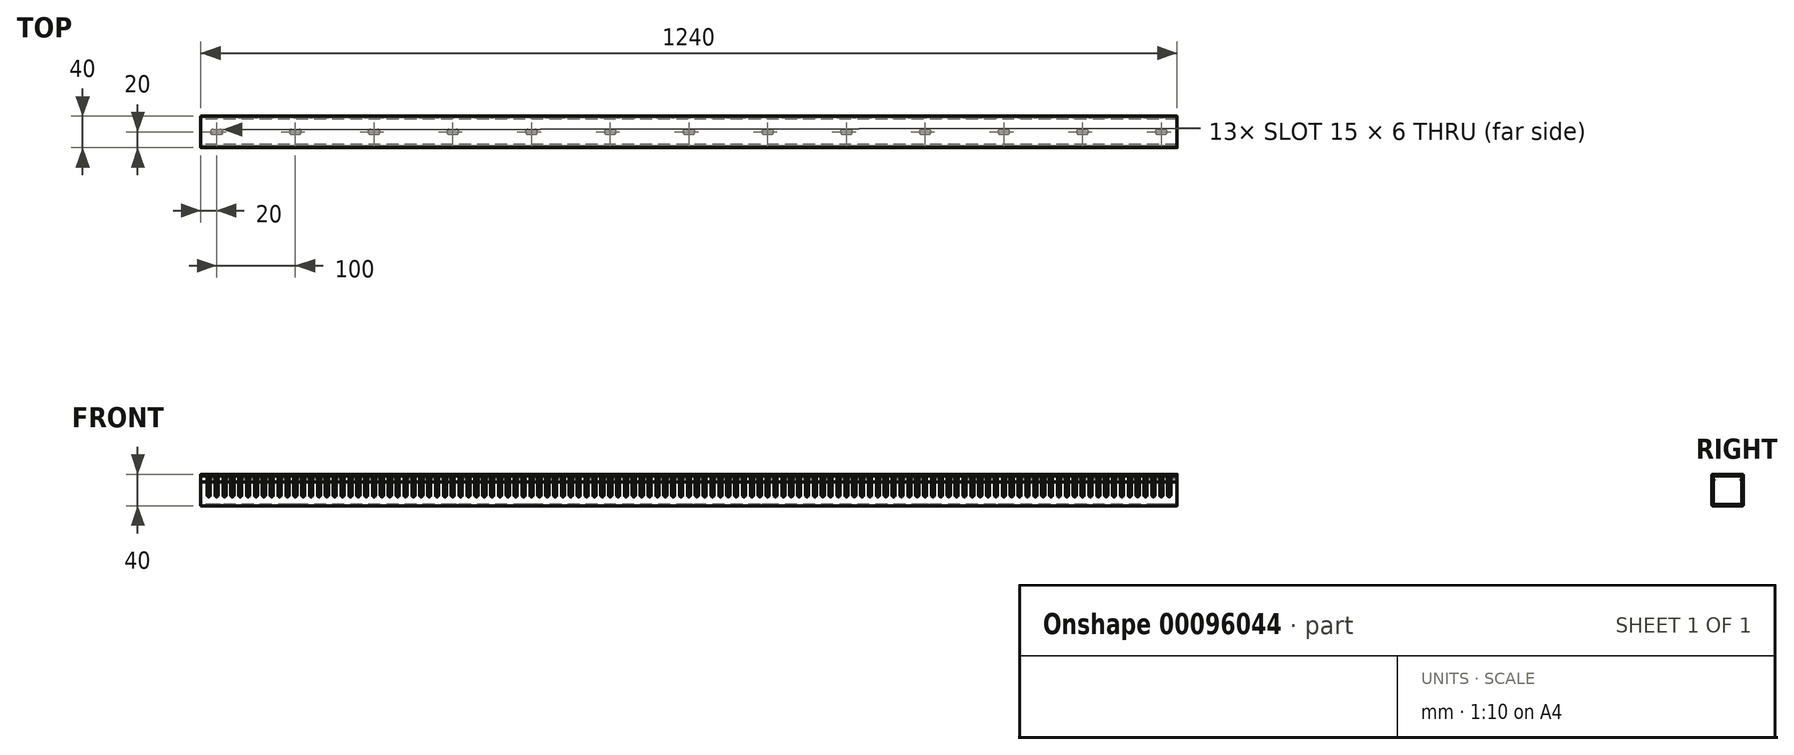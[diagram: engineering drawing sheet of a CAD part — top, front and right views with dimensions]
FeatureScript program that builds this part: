
annotation { "Feature Type Name" : "Feature", "Feature Type Description" : "" }
export const myFeature = defineFeature(function(context is Context, id is Id, definition is map)
    precondition{}
    {
        {
            var Q0;
            Q0=qCreatedBy(makeId("Right.planeOp"),FACE);
            var sketch = newSketch(context, id + "F0", { "sketchPlane" : qUnion([Q0])});
            skLineSegment(sketch, "E0", {"start": v(-20, 0) * mm, "end": v(-20, 38) * mm});
            skLineSegment(sketch, "E1", {"start": v(-20, 38) * mm, "end": v(-18, 38) * mm});
            skLineSegment(sketch, "E2", {"start": v(-18, 38) * mm, "end": v(-18, 2) * mm});
            skLineSegment(sketch, "E3", {"start": v(-18, 2) * mm, "end": v(18, 2) * mm});
            skLineSegment(sketch, "E4", {"start": v(18, 2) * mm, "end": v(18, 38) * mm});
            skLineSegment(sketch, "E5", {"start": v(18, 38) * mm, "end": v(20, 38) * mm});
            skLineSegment(sketch, "E6", {"start": v(20, 38) * mm, "end": v(20, 0) * mm});
            skLineSegment(sketch, "E7", {"start": v(20, 0) * mm, "end": v(-20, 0) * mm});
            skSolve(sketch);
        }
        {
            var Q0;
            Q0 = qSketchRegion(id + "F0", true);
            extrude(context, id + "F1", {"entities" : qUnion([Q0]), "endBound" : BoundingType.SYMMETRIC, "depth" : 1240 * mm});
        }
        {
            var Q0;
            Q0=makeQuery(id+"F1.opExtrude","SWEPT_FACE",FACE,{"disambiguationData":[OSD([sQuery(id+"F0.wireOp",EDGE,"E0")])]});
            var sketch = newSketch(context, id + "F2", { "sketchPlane" : qUnion([Q0])});
            skLineSegment(sketch, "E8.bottom", {"start": v(-2, 38) * mm, "end": v(2, 38) * mm});
            skLineSegment(sketch, "E8.left", {"start": v(-2, 38) * mm, "end": v(-2, 13.4) * mm});
            skLineSegment(sketch, "E8.right", {"start": v(2, 38) * mm, "end": v(2, 13.4) * mm});
            skArc(sketch, "E9", {"start": v(-2, 13.4) * mm, "mid": v(0, 11.4) * mm, "end": v(2, 13.4) * mm});
            skLineSegment(sketch, "E10.1.0.0", {"start": v(8, 38) * mm, "end": v(12, 38) * mm});
            skLineSegment(sketch, "E10.1.0.1", {"start": v(8, 38) * mm, "end": v(8, 13.4) * mm});
            skLineSegment(sketch, "E10.1.0.2", {"start": v(12, 38) * mm, "end": v(12, 13.4) * mm});
            skArc(sketch, "E10.1.0.3", {"start": v(8, 13.4) * mm, "mid": v(10, 11.4) * mm, "end": v(12, 13.4) * mm});
            skLineSegment(sketch, "E10.2.0.0", {"start": v(18, 38) * mm, "end": v(22, 38) * mm});
            skLineSegment(sketch, "E10.2.0.1", {"start": v(18, 38) * mm, "end": v(18, 13.4) * mm});
            skLineSegment(sketch, "E10.2.0.2", {"start": v(22, 38) * mm, "end": v(22, 13.4) * mm});
            skArc(sketch, "E10.2.0.3", {"start": v(18, 13.4) * mm, "mid": v(20, 11.4) * mm, "end": v(22, 13.4) * mm});
            skLineSegment(sketch, "E10.3.0.0", {"start": v(28, 38) * mm, "end": v(32, 38) * mm});
            skLineSegment(sketch, "E10.3.0.1", {"start": v(28, 38) * mm, "end": v(28, 13.4) * mm});
            skLineSegment(sketch, "E10.3.0.2", {"start": v(32, 38) * mm, "end": v(32, 13.4) * mm});
            skArc(sketch, "E10.3.0.3", {"start": v(28, 13.4) * mm, "mid": v(30, 11.4) * mm, "end": v(32, 13.4) * mm});
            skLineSegment(sketch, "E10.4.0.0", {"start": v(38, 38) * mm, "end": v(42, 38) * mm});
            skLineSegment(sketch, "E10.4.0.1", {"start": v(38, 38) * mm, "end": v(38, 13.4) * mm});
            skLineSegment(sketch, "E10.4.0.2", {"start": v(42, 38) * mm, "end": v(42, 13.4) * mm});
            skArc(sketch, "E10.4.0.3", {"start": v(38, 13.4) * mm, "mid": v(40, 11.4) * mm, "end": v(42, 13.4) * mm});
            skLineSegment(sketch, "E10.5.0.0", {"start": v(48, 38) * mm, "end": v(52, 38) * mm});
            skLineSegment(sketch, "E10.5.0.1", {"start": v(48, 38) * mm, "end": v(48, 13.4) * mm});
            skLineSegment(sketch, "E10.5.0.2", {"start": v(52, 38) * mm, "end": v(52, 13.4) * mm});
            skArc(sketch, "E10.5.0.3", {"start": v(48, 13.4) * mm, "mid": v(50, 11.4) * mm, "end": v(52, 13.4) * mm});
            skLineSegment(sketch, "E10.6.0.0", {"start": v(58, 38) * mm, "end": v(62, 38) * mm});
            skLineSegment(sketch, "E10.6.0.1", {"start": v(58, 38) * mm, "end": v(58, 13.4) * mm});
            skLineSegment(sketch, "E10.6.0.2", {"start": v(62, 38) * mm, "end": v(62, 13.4) * mm});
            skArc(sketch, "E10.6.0.3", {"start": v(58, 13.4) * mm, "mid": v(60, 11.4) * mm, "end": v(62, 13.4) * mm});
            skLineSegment(sketch, "E10.7.0.0", {"start": v(68, 38) * mm, "end": v(72, 38) * mm});
            skLineSegment(sketch, "E10.7.0.1", {"start": v(68, 38) * mm, "end": v(68, 13.4) * mm});
            skLineSegment(sketch, "E10.7.0.2", {"start": v(72, 38) * mm, "end": v(72, 13.4) * mm});
            skArc(sketch, "E10.7.0.3", {"start": v(68, 13.4) * mm, "mid": v(70, 11.4) * mm, "end": v(72, 13.4) * mm});
            skLineSegment(sketch, "E10.8.0.0", {"start": v(78, 38) * mm, "end": v(82, 38) * mm});
            skLineSegment(sketch, "E10.8.0.1", {"start": v(78, 38) * mm, "end": v(78, 13.4) * mm});
            skLineSegment(sketch, "E10.8.0.2", {"start": v(82, 38) * mm, "end": v(82, 13.4) * mm});
            skArc(sketch, "E10.8.0.3", {"start": v(78, 13.4) * mm, "mid": v(80, 11.4) * mm, "end": v(82, 13.4) * mm});
            skLineSegment(sketch, "E10.9.0.0", {"start": v(88, 38) * mm, "end": v(92, 38) * mm});
            skLineSegment(sketch, "E10.9.0.1", {"start": v(88, 38) * mm, "end": v(88, 13.4) * mm});
            skLineSegment(sketch, "E10.9.0.2", {"start": v(92, 38) * mm, "end": v(92, 13.4) * mm});
            skArc(sketch, "E10.9.0.3", {"start": v(88, 13.4) * mm, "mid": v(90, 11.4) * mm, "end": v(92, 13.4) * mm});
            skLineSegment(sketch, "E10.10.0.0", {"start": v(98, 38) * mm, "end": v(102, 38) * mm});
            skLineSegment(sketch, "E10.10.0.1", {"start": v(98, 38) * mm, "end": v(98, 13.4) * mm});
            skLineSegment(sketch, "E10.10.0.2", {"start": v(102, 38) * mm, "end": v(102, 13.4) * mm});
            skArc(sketch, "E10.10.0.3", {"start": v(98, 13.4) * mm, "mid": v(100, 11.4) * mm, "end": v(102, 13.4) * mm});
            skLineSegment(sketch, "E10.11.0.0", {"start": v(108, 38) * mm, "end": v(112, 38) * mm});
            skLineSegment(sketch, "E10.11.0.1", {"start": v(108, 38) * mm, "end": v(108, 13.4) * mm});
            skLineSegment(sketch, "E10.11.0.2", {"start": v(112, 38) * mm, "end": v(112, 13.4) * mm});
            skArc(sketch, "E10.11.0.3", {"start": v(108, 13.4) * mm, "mid": v(110, 11.4) * mm, "end": v(112, 13.4) * mm});
            skLineSegment(sketch, "E10.12.0.0", {"start": v(118, 38) * mm, "end": v(122, 38) * mm});
            skLineSegment(sketch, "E10.12.0.1", {"start": v(118, 38) * mm, "end": v(118, 13.4) * mm});
            skLineSegment(sketch, "E10.12.0.2", {"start": v(122, 38) * mm, "end": v(122, 13.4) * mm});
            skArc(sketch, "E10.12.0.3", {"start": v(118, 13.4) * mm, "mid": v(120, 11.4) * mm, "end": v(122, 13.4) * mm});
            skLineSegment(sketch, "E10.13.0.0", {"start": v(128, 38) * mm, "end": v(132, 38) * mm});
            skLineSegment(sketch, "E10.13.0.1", {"start": v(128, 38) * mm, "end": v(128, 13.4) * mm});
            skLineSegment(sketch, "E10.13.0.2", {"start": v(132, 38) * mm, "end": v(132, 13.4) * mm});
            skArc(sketch, "E10.13.0.3", {"start": v(128, 13.4) * mm, "mid": v(130, 11.4) * mm, "end": v(132, 13.4) * mm});
            skLineSegment(sketch, "E10.14.0.0", {"start": v(138, 38) * mm, "end": v(142, 38) * mm});
            skLineSegment(sketch, "E10.14.0.1", {"start": v(138, 38) * mm, "end": v(138, 13.4) * mm});
            skLineSegment(sketch, "E10.14.0.2", {"start": v(142, 38) * mm, "end": v(142, 13.4) * mm});
            skArc(sketch, "E10.14.0.3", {"start": v(138, 13.4) * mm, "mid": v(140, 11.4) * mm, "end": v(142, 13.4) * mm});
            skLineSegment(sketch, "E10.15.0.0", {"start": v(148, 38) * mm, "end": v(152, 38) * mm});
            skLineSegment(sketch, "E10.15.0.1", {"start": v(148, 38) * mm, "end": v(148, 13.4) * mm});
            skLineSegment(sketch, "E10.15.0.2", {"start": v(152, 38) * mm, "end": v(152, 13.4) * mm});
            skArc(sketch, "E10.15.0.3", {"start": v(148, 13.4) * mm, "mid": v(150, 11.4) * mm, "end": v(152, 13.4) * mm});
            skLineSegment(sketch, "E10.16.0.0", {"start": v(158, 38) * mm, "end": v(162, 38) * mm});
            skLineSegment(sketch, "E10.16.0.1", {"start": v(158, 38) * mm, "end": v(158, 13.4) * mm});
            skLineSegment(sketch, "E10.16.0.2", {"start": v(162, 38) * mm, "end": v(162, 13.4) * mm});
            skArc(sketch, "E10.16.0.3", {"start": v(158, 13.4) * mm, "mid": v(160, 11.4) * mm, "end": v(162, 13.4) * mm});
            skLineSegment(sketch, "E10.17.0.0", {"start": v(168, 38) * mm, "end": v(172, 38) * mm});
            skLineSegment(sketch, "E10.17.0.1", {"start": v(168, 38) * mm, "end": v(168, 13.4) * mm});
            skLineSegment(sketch, "E10.17.0.2", {"start": v(172, 38) * mm, "end": v(172, 13.4) * mm});
            skArc(sketch, "E10.17.0.3", {"start": v(168, 13.4) * mm, "mid": v(170, 11.4) * mm, "end": v(172, 13.4) * mm});
            skLineSegment(sketch, "E10.18.0.0", {"start": v(178, 38) * mm, "end": v(182, 38) * mm});
            skLineSegment(sketch, "E10.18.0.1", {"start": v(178, 38) * mm, "end": v(178, 13.4) * mm});
            skLineSegment(sketch, "E10.18.0.2", {"start": v(182, 38) * mm, "end": v(182, 13.4) * mm});
            skArc(sketch, "E10.18.0.3", {"start": v(178, 13.4) * mm, "mid": v(180, 11.4) * mm, "end": v(182, 13.4) * mm});
            skLineSegment(sketch, "E10.19.0.0", {"start": v(188, 38) * mm, "end": v(192, 38) * mm});
            skLineSegment(sketch, "E10.19.0.1", {"start": v(188, 38) * mm, "end": v(188, 13.4) * mm});
            skLineSegment(sketch, "E10.19.0.2", {"start": v(192, 38) * mm, "end": v(192, 13.4) * mm});
            skArc(sketch, "E10.19.0.3", {"start": v(188, 13.4) * mm, "mid": v(190, 11.4) * mm, "end": v(192, 13.4) * mm});
            skLineSegment(sketch, "E10.20.0.0", {"start": v(198, 38) * mm, "end": v(202, 38) * mm});
            skLineSegment(sketch, "E10.20.0.1", {"start": v(198, 38) * mm, "end": v(198, 13.4) * mm});
            skLineSegment(sketch, "E10.20.0.2", {"start": v(202, 38) * mm, "end": v(202, 13.4) * mm});
            skArc(sketch, "E10.20.0.3", {"start": v(198, 13.4) * mm, "mid": v(200, 11.4) * mm, "end": v(202, 13.4) * mm});
            skLineSegment(sketch, "E10.21.0.0", {"start": v(208, 38) * mm, "end": v(212, 38) * mm});
            skLineSegment(sketch, "E10.21.0.1", {"start": v(208, 38) * mm, "end": v(208, 13.4) * mm});
            skLineSegment(sketch, "E10.21.0.2", {"start": v(212, 38) * mm, "end": v(212, 13.4) * mm});
            skArc(sketch, "E10.21.0.3", {"start": v(208, 13.4) * mm, "mid": v(210, 11.4) * mm, "end": v(212, 13.4) * mm});
            skLineSegment(sketch, "E10.22.0.0", {"start": v(218, 38) * mm, "end": v(222, 38) * mm});
            skLineSegment(sketch, "E10.22.0.1", {"start": v(218, 38) * mm, "end": v(218, 13.4) * mm});
            skLineSegment(sketch, "E10.22.0.2", {"start": v(222, 38) * mm, "end": v(222, 13.4) * mm});
            skArc(sketch, "E10.22.0.3", {"start": v(218, 13.4) * mm, "mid": v(220, 11.4) * mm, "end": v(222, 13.4) * mm});
            skLineSegment(sketch, "E10.23.0.0", {"start": v(228, 38) * mm, "end": v(232, 38) * mm});
            skLineSegment(sketch, "E10.23.0.1", {"start": v(228, 38) * mm, "end": v(228, 13.4) * mm});
            skLineSegment(sketch, "E10.23.0.2", {"start": v(232, 38) * mm, "end": v(232, 13.4) * mm});
            skArc(sketch, "E10.23.0.3", {"start": v(228, 13.4) * mm, "mid": v(230, 11.4) * mm, "end": v(232, 13.4) * mm});
            skLineSegment(sketch, "E10.24.0.0", {"start": v(238, 38) * mm, "end": v(242, 38) * mm});
            skLineSegment(sketch, "E10.24.0.1", {"start": v(238, 38) * mm, "end": v(238, 13.4) * mm});
            skLineSegment(sketch, "E10.24.0.2", {"start": v(242, 38) * mm, "end": v(242, 13.4) * mm});
            skArc(sketch, "E10.24.0.3", {"start": v(238, 13.4) * mm, "mid": v(240, 11.4) * mm, "end": v(242, 13.4) * mm});
            skLineSegment(sketch, "E10.25.0.0", {"start": v(248, 38) * mm, "end": v(252, 38) * mm});
            skLineSegment(sketch, "E10.25.0.1", {"start": v(248, 38) * mm, "end": v(248, 13.4) * mm});
            skLineSegment(sketch, "E10.25.0.2", {"start": v(252, 38) * mm, "end": v(252, 13.4) * mm});
            skArc(sketch, "E10.25.0.3", {"start": v(248, 13.4) * mm, "mid": v(250, 11.4) * mm, "end": v(252, 13.4) * mm});
            skLineSegment(sketch, "E10.26.0.0", {"start": v(258, 38) * mm, "end": v(262, 38) * mm});
            skLineSegment(sketch, "E10.26.0.1", {"start": v(258, 38) * mm, "end": v(258, 13.4) * mm});
            skLineSegment(sketch, "E10.26.0.2", {"start": v(262, 38) * mm, "end": v(262, 13.4) * mm});
            skArc(sketch, "E10.26.0.3", {"start": v(258, 13.4) * mm, "mid": v(260, 11.4) * mm, "end": v(262, 13.4) * mm});
            skLineSegment(sketch, "E10.27.0.0", {"start": v(268, 38) * mm, "end": v(272, 38) * mm});
            skLineSegment(sketch, "E10.27.0.1", {"start": v(268, 38) * mm, "end": v(268, 13.4) * mm});
            skLineSegment(sketch, "E10.27.0.2", {"start": v(272, 38) * mm, "end": v(272, 13.4) * mm});
            skArc(sketch, "E10.27.0.3", {"start": v(268, 13.4) * mm, "mid": v(270, 11.4) * mm, "end": v(272, 13.4) * mm});
            skLineSegment(sketch, "E10.28.0.0", {"start": v(278, 38) * mm, "end": v(282, 38) * mm});
            skLineSegment(sketch, "E10.28.0.1", {"start": v(278, 38) * mm, "end": v(278, 13.4) * mm});
            skLineSegment(sketch, "E10.28.0.2", {"start": v(282, 38) * mm, "end": v(282, 13.4) * mm});
            skArc(sketch, "E10.28.0.3", {"start": v(278, 13.4) * mm, "mid": v(280, 11.4) * mm, "end": v(282, 13.4) * mm});
            skLineSegment(sketch, "E10.29.0.0", {"start": v(288, 38) * mm, "end": v(292, 38) * mm});
            skLineSegment(sketch, "E10.29.0.1", {"start": v(288, 38) * mm, "end": v(288, 13.4) * mm});
            skLineSegment(sketch, "E10.29.0.2", {"start": v(292, 38) * mm, "end": v(292, 13.4) * mm});
            skArc(sketch, "E10.29.0.3", {"start": v(288, 13.4) * mm, "mid": v(290, 11.4) * mm, "end": v(292, 13.4) * mm});
            skLineSegment(sketch, "E10.30.0.0", {"start": v(298, 38) * mm, "end": v(302, 38) * mm});
            skLineSegment(sketch, "E10.30.0.1", {"start": v(298, 38) * mm, "end": v(298, 13.4) * mm});
            skLineSegment(sketch, "E10.30.0.2", {"start": v(302, 38) * mm, "end": v(302, 13.4) * mm});
            skArc(sketch, "E10.30.0.3", {"start": v(298, 13.4) * mm, "mid": v(300, 11.4) * mm, "end": v(302, 13.4) * mm});
            skLineSegment(sketch, "E10.31.0.0", {"start": v(308, 38) * mm, "end": v(312, 38) * mm});
            skLineSegment(sketch, "E10.31.0.1", {"start": v(308, 38) * mm, "end": v(308, 13.4) * mm});
            skLineSegment(sketch, "E10.31.0.2", {"start": v(312, 38) * mm, "end": v(312, 13.4) * mm});
            skArc(sketch, "E10.31.0.3", {"start": v(308, 13.4) * mm, "mid": v(310, 11.4) * mm, "end": v(312, 13.4) * mm});
            skLineSegment(sketch, "E10.32.0.0", {"start": v(318, 38) * mm, "end": v(322, 38) * mm});
            skLineSegment(sketch, "E10.32.0.1", {"start": v(318, 38) * mm, "end": v(318, 13.4) * mm});
            skLineSegment(sketch, "E10.32.0.2", {"start": v(322, 38) * mm, "end": v(322, 13.4) * mm});
            skArc(sketch, "E10.32.0.3", {"start": v(318, 13.4) * mm, "mid": v(320, 11.4) * mm, "end": v(322, 13.4) * mm});
            skLineSegment(sketch, "E10.33.0.0", {"start": v(328, 38) * mm, "end": v(332, 38) * mm});
            skLineSegment(sketch, "E10.33.0.1", {"start": v(328, 38) * mm, "end": v(328, 13.4) * mm});
            skLineSegment(sketch, "E10.33.0.2", {"start": v(332, 38) * mm, "end": v(332, 13.4) * mm});
            skArc(sketch, "E10.33.0.3", {"start": v(328, 13.4) * mm, "mid": v(330, 11.4) * mm, "end": v(332, 13.4) * mm});
            skLineSegment(sketch, "E10.34.0.0", {"start": v(338, 38) * mm, "end": v(342, 38) * mm});
            skLineSegment(sketch, "E10.34.0.1", {"start": v(338, 38) * mm, "end": v(338, 13.4) * mm});
            skLineSegment(sketch, "E10.34.0.2", {"start": v(342, 38) * mm, "end": v(342, 13.4) * mm});
            skArc(sketch, "E10.34.0.3", {"start": v(338, 13.4) * mm, "mid": v(340, 11.4) * mm, "end": v(342, 13.4) * mm});
            skLineSegment(sketch, "E10.35.0.0", {"start": v(348, 38) * mm, "end": v(352, 38) * mm});
            skLineSegment(sketch, "E10.35.0.1", {"start": v(348, 38) * mm, "end": v(348, 13.4) * mm});
            skLineSegment(sketch, "E10.35.0.2", {"start": v(352, 38) * mm, "end": v(352, 13.4) * mm});
            skArc(sketch, "E10.35.0.3", {"start": v(348, 13.4) * mm, "mid": v(350, 11.4) * mm, "end": v(352, 13.4) * mm});
            skLineSegment(sketch, "E10.36.0.0", {"start": v(358, 38) * mm, "end": v(362, 38) * mm});
            skLineSegment(sketch, "E10.36.0.1", {"start": v(358, 38) * mm, "end": v(358, 13.4) * mm});
            skLineSegment(sketch, "E10.36.0.2", {"start": v(362, 38) * mm, "end": v(362, 13.4) * mm});
            skArc(sketch, "E10.36.0.3", {"start": v(358, 13.4) * mm, "mid": v(360, 11.4) * mm, "end": v(362, 13.4) * mm});
            skLineSegment(sketch, "E10.37.0.0", {"start": v(368, 38) * mm, "end": v(372, 38) * mm});
            skLineSegment(sketch, "E10.37.0.1", {"start": v(368, 38) * mm, "end": v(368, 13.4) * mm});
            skLineSegment(sketch, "E10.37.0.2", {"start": v(372, 38) * mm, "end": v(372, 13.4) * mm});
            skArc(sketch, "E10.37.0.3", {"start": v(368, 13.4) * mm, "mid": v(370, 11.4) * mm, "end": v(372, 13.4) * mm});
            skLineSegment(sketch, "E10.38.0.0", {"start": v(378, 38) * mm, "end": v(382, 38) * mm});
            skLineSegment(sketch, "E10.38.0.1", {"start": v(378, 38) * mm, "end": v(378, 13.4) * mm});
            skLineSegment(sketch, "E10.38.0.2", {"start": v(382, 38) * mm, "end": v(382, 13.4) * mm});
            skArc(sketch, "E10.38.0.3", {"start": v(378, 13.4) * mm, "mid": v(380, 11.4) * mm, "end": v(382, 13.4) * mm});
            skLineSegment(sketch, "E10.39.0.0", {"start": v(388, 38) * mm, "end": v(392, 38) * mm});
            skLineSegment(sketch, "E10.39.0.1", {"start": v(388, 38) * mm, "end": v(388, 13.4) * mm});
            skLineSegment(sketch, "E10.39.0.2", {"start": v(392, 38) * mm, "end": v(392, 13.4) * mm});
            skArc(sketch, "E10.39.0.3", {"start": v(388, 13.4) * mm, "mid": v(390, 11.4) * mm, "end": v(392, 13.4) * mm});
            skLineSegment(sketch, "E10.40.0.0", {"start": v(398, 38) * mm, "end": v(402, 38) * mm});
            skLineSegment(sketch, "E10.40.0.1", {"start": v(398, 38) * mm, "end": v(398, 13.4) * mm});
            skLineSegment(sketch, "E10.40.0.2", {"start": v(402, 38) * mm, "end": v(402, 13.4) * mm});
            skArc(sketch, "E10.40.0.3", {"start": v(398, 13.4) * mm, "mid": v(400, 11.4) * mm, "end": v(402, 13.4) * mm});
            skLineSegment(sketch, "E10.41.0.0", {"start": v(408, 38) * mm, "end": v(412, 38) * mm});
            skLineSegment(sketch, "E10.41.0.1", {"start": v(408, 38) * mm, "end": v(408, 13.4) * mm});
            skLineSegment(sketch, "E10.41.0.2", {"start": v(412, 38) * mm, "end": v(412, 13.4) * mm});
            skArc(sketch, "E10.41.0.3", {"start": v(408, 13.4) * mm, "mid": v(410, 11.4) * mm, "end": v(412, 13.4) * mm});
            skLineSegment(sketch, "E10.42.0.0", {"start": v(418, 38) * mm, "end": v(422, 38) * mm});
            skLineSegment(sketch, "E10.42.0.1", {"start": v(418, 38) * mm, "end": v(418, 13.4) * mm});
            skLineSegment(sketch, "E10.42.0.2", {"start": v(422, 38) * mm, "end": v(422, 13.4) * mm});
            skArc(sketch, "E10.42.0.3", {"start": v(418, 13.4) * mm, "mid": v(420, 11.4) * mm, "end": v(422, 13.4) * mm});
            skLineSegment(sketch, "E10.43.0.0", {"start": v(428, 38) * mm, "end": v(432, 38) * mm});
            skLineSegment(sketch, "E10.43.0.1", {"start": v(428, 38) * mm, "end": v(428, 13.4) * mm});
            skLineSegment(sketch, "E10.43.0.2", {"start": v(432, 38) * mm, "end": v(432, 13.4) * mm});
            skArc(sketch, "E10.43.0.3", {"start": v(428, 13.4) * mm, "mid": v(430, 11.4) * mm, "end": v(432, 13.4) * mm});
            skLineSegment(sketch, "E10.44.0.0", {"start": v(438, 38) * mm, "end": v(442, 38) * mm});
            skLineSegment(sketch, "E10.44.0.1", {"start": v(438, 38) * mm, "end": v(438, 13.4) * mm});
            skLineSegment(sketch, "E10.44.0.2", {"start": v(442, 38) * mm, "end": v(442, 13.4) * mm});
            skArc(sketch, "E10.44.0.3", {"start": v(438, 13.4) * mm, "mid": v(440, 11.4) * mm, "end": v(442, 13.4) * mm});
            skLineSegment(sketch, "E10.45.0.0", {"start": v(448, 38) * mm, "end": v(452, 38) * mm});
            skLineSegment(sketch, "E10.45.0.1", {"start": v(448, 38) * mm, "end": v(448, 13.4) * mm});
            skLineSegment(sketch, "E10.45.0.2", {"start": v(452, 38) * mm, "end": v(452, 13.4) * mm});
            skArc(sketch, "E10.45.0.3", {"start": v(448, 13.4) * mm, "mid": v(450, 11.4) * mm, "end": v(452, 13.4) * mm});
            skLineSegment(sketch, "E10.46.0.0", {"start": v(458, 38) * mm, "end": v(462, 38) * mm});
            skLineSegment(sketch, "E10.46.0.1", {"start": v(458, 38) * mm, "end": v(458, 13.4) * mm});
            skLineSegment(sketch, "E10.46.0.2", {"start": v(462, 38) * mm, "end": v(462, 13.4) * mm});
            skArc(sketch, "E10.46.0.3", {"start": v(458, 13.4) * mm, "mid": v(460, 11.4) * mm, "end": v(462, 13.4) * mm});
            skLineSegment(sketch, "E10.47.0.0", {"start": v(468, 38) * mm, "end": v(472, 38) * mm});
            skLineSegment(sketch, "E10.47.0.1", {"start": v(468, 38) * mm, "end": v(468, 13.4) * mm});
            skLineSegment(sketch, "E10.47.0.2", {"start": v(472, 38) * mm, "end": v(472, 13.4) * mm});
            skArc(sketch, "E10.47.0.3", {"start": v(468, 13.4) * mm, "mid": v(470, 11.4) * mm, "end": v(472, 13.4) * mm});
            skLineSegment(sketch, "E10.48.0.0", {"start": v(478, 38) * mm, "end": v(482, 38) * mm});
            skLineSegment(sketch, "E10.48.0.1", {"start": v(478, 38) * mm, "end": v(478, 13.4) * mm});
            skLineSegment(sketch, "E10.48.0.2", {"start": v(482, 38) * mm, "end": v(482, 13.4) * mm});
            skArc(sketch, "E10.48.0.3", {"start": v(478, 13.4) * mm, "mid": v(480, 11.4) * mm, "end": v(482, 13.4) * mm});
            skLineSegment(sketch, "E10.49.0.0", {"start": v(488, 38) * mm, "end": v(492, 38) * mm});
            skLineSegment(sketch, "E10.49.0.1", {"start": v(488, 38) * mm, "end": v(488, 13.4) * mm});
            skLineSegment(sketch, "E10.49.0.2", {"start": v(492, 38) * mm, "end": v(492, 13.4) * mm});
            skArc(sketch, "E10.49.0.3", {"start": v(488, 13.4) * mm, "mid": v(490, 11.4) * mm, "end": v(492, 13.4) * mm});
            skLineSegment(sketch, "E10.direction1", {"start": v(-2, 38) * mm, "end": v(8, 38) * mm, "construction": true});
            skLineSegment(sketch, "E11.1.0.0", {"start": v(-12, 38) * mm, "end": v(-8, 38) * mm});
            skLineSegment(sketch, "E11.1.0.1", {"start": v(-12, 38) * mm, "end": v(-12, 13.4) * mm});
            skLineSegment(sketch, "E11.1.0.2", {"start": v(-8, 38) * mm, "end": v(-8, 13.4) * mm});
            skArc(sketch, "E11.1.0.3", {"start": v(-12, 13.4) * mm, "mid": v(-10, 11.4) * mm, "end": v(-8, 13.4) * mm});
            skLineSegment(sketch, "E11.2.0.0", {"start": v(-22, 38) * mm, "end": v(-18, 38) * mm});
            skLineSegment(sketch, "E11.2.0.1", {"start": v(-22, 38) * mm, "end": v(-22, 13.4) * mm});
            skLineSegment(sketch, "E11.2.0.2", {"start": v(-18, 38) * mm, "end": v(-18, 13.4) * mm});
            skArc(sketch, "E11.2.0.3", {"start": v(-22, 13.4) * mm, "mid": v(-20, 11.4) * mm, "end": v(-18, 13.4) * mm});
            skLineSegment(sketch, "E11.3.0.0", {"start": v(-32, 38) * mm, "end": v(-28, 38) * mm});
            skLineSegment(sketch, "E11.3.0.1", {"start": v(-32, 38) * mm, "end": v(-32, 13.4) * mm});
            skLineSegment(sketch, "E11.3.0.2", {"start": v(-28, 38) * mm, "end": v(-28, 13.4) * mm});
            skArc(sketch, "E11.3.0.3", {"start": v(-32, 13.4) * mm, "mid": v(-30, 11.4) * mm, "end": v(-28, 13.4) * mm});
            skLineSegment(sketch, "E11.4.0.0", {"start": v(-42, 38) * mm, "end": v(-38, 38) * mm});
            skLineSegment(sketch, "E11.4.0.1", {"start": v(-42, 38) * mm, "end": v(-42, 13.4) * mm});
            skLineSegment(sketch, "E11.4.0.2", {"start": v(-38, 38) * mm, "end": v(-38, 13.4) * mm});
            skArc(sketch, "E11.4.0.3", {"start": v(-42, 13.4) * mm, "mid": v(-40, 11.4) * mm, "end": v(-38, 13.4) * mm});
            skLineSegment(sketch, "E11.5.0.0", {"start": v(-52, 38) * mm, "end": v(-48, 38) * mm});
            skLineSegment(sketch, "E11.5.0.1", {"start": v(-52, 38) * mm, "end": v(-52, 13.4) * mm});
            skLineSegment(sketch, "E11.5.0.2", {"start": v(-48, 38) * mm, "end": v(-48, 13.4) * mm});
            skArc(sketch, "E11.5.0.3", {"start": v(-52, 13.4) * mm, "mid": v(-50, 11.4) * mm, "end": v(-48, 13.4) * mm});
            skLineSegment(sketch, "E11.6.0.0", {"start": v(-62, 38) * mm, "end": v(-58, 38) * mm});
            skLineSegment(sketch, "E11.6.0.1", {"start": v(-62, 38) * mm, "end": v(-62, 13.4) * mm});
            skLineSegment(sketch, "E11.6.0.2", {"start": v(-58, 38) * mm, "end": v(-58, 13.4) * mm});
            skArc(sketch, "E11.6.0.3", {"start": v(-62, 13.4) * mm, "mid": v(-60, 11.4) * mm, "end": v(-58, 13.4) * mm});
            skLineSegment(sketch, "E11.7.0.0", {"start": v(-72, 38) * mm, "end": v(-68, 38) * mm});
            skLineSegment(sketch, "E11.7.0.1", {"start": v(-72, 38) * mm, "end": v(-72, 13.4) * mm});
            skLineSegment(sketch, "E11.7.0.2", {"start": v(-68, 38) * mm, "end": v(-68, 13.4) * mm});
            skArc(sketch, "E11.7.0.3", {"start": v(-72, 13.4) * mm, "mid": v(-70, 11.4) * mm, "end": v(-68, 13.4) * mm});
            skLineSegment(sketch, "E11.8.0.0", {"start": v(-82, 38) * mm, "end": v(-78, 38) * mm});
            skLineSegment(sketch, "E11.8.0.1", {"start": v(-82, 38) * mm, "end": v(-82, 13.4) * mm});
            skLineSegment(sketch, "E11.8.0.2", {"start": v(-78, 38) * mm, "end": v(-78, 13.4) * mm});
            skArc(sketch, "E11.8.0.3", {"start": v(-82, 13.4) * mm, "mid": v(-80, 11.4) * mm, "end": v(-78, 13.4) * mm});
            skLineSegment(sketch, "E11.9.0.0", {"start": v(-92, 38) * mm, "end": v(-88, 38) * mm});
            skLineSegment(sketch, "E11.9.0.1", {"start": v(-92, 38) * mm, "end": v(-92, 13.4) * mm});
            skLineSegment(sketch, "E11.9.0.2", {"start": v(-88, 38) * mm, "end": v(-88, 13.4) * mm});
            skArc(sketch, "E11.9.0.3", {"start": v(-92, 13.4) * mm, "mid": v(-90, 11.4) * mm, "end": v(-88, 13.4) * mm});
            skLineSegment(sketch, "E11.10.0.0", {"start": v(-102, 38) * mm, "end": v(-98, 38) * mm});
            skLineSegment(sketch, "E11.10.0.1", {"start": v(-102, 38) * mm, "end": v(-102, 13.4) * mm});
            skLineSegment(sketch, "E11.10.0.2", {"start": v(-98, 38) * mm, "end": v(-98, 13.4) * mm});
            skArc(sketch, "E11.10.0.3", {"start": v(-102, 13.4) * mm, "mid": v(-100, 11.4) * mm, "end": v(-98, 13.4) * mm});
            skLineSegment(sketch, "E11.11.0.0", {"start": v(-112, 38) * mm, "end": v(-108, 38) * mm});
            skLineSegment(sketch, "E11.11.0.1", {"start": v(-112, 38) * mm, "end": v(-112, 13.4) * mm});
            skLineSegment(sketch, "E11.11.0.2", {"start": v(-108, 38) * mm, "end": v(-108, 13.4) * mm});
            skArc(sketch, "E11.11.0.3", {"start": v(-112, 13.4) * mm, "mid": v(-110, 11.4) * mm, "end": v(-108, 13.4) * mm});
            skLineSegment(sketch, "E11.12.0.0", {"start": v(-122, 38) * mm, "end": v(-118, 38) * mm});
            skLineSegment(sketch, "E11.12.0.1", {"start": v(-122, 38) * mm, "end": v(-122, 13.4) * mm});
            skLineSegment(sketch, "E11.12.0.2", {"start": v(-118, 38) * mm, "end": v(-118, 13.4) * mm});
            skArc(sketch, "E11.12.0.3", {"start": v(-122, 13.4) * mm, "mid": v(-120, 11.4) * mm, "end": v(-118, 13.4) * mm});
            skLineSegment(sketch, "E11.13.0.0", {"start": v(-132, 38) * mm, "end": v(-128, 38) * mm});
            skLineSegment(sketch, "E11.13.0.1", {"start": v(-132, 38) * mm, "end": v(-132, 13.4) * mm});
            skLineSegment(sketch, "E11.13.0.2", {"start": v(-128, 38) * mm, "end": v(-128, 13.4) * mm});
            skArc(sketch, "E11.13.0.3", {"start": v(-132, 13.4) * mm, "mid": v(-130, 11.4) * mm, "end": v(-128, 13.4) * mm});
            skLineSegment(sketch, "E11.14.0.0", {"start": v(-142, 38) * mm, "end": v(-138, 38) * mm});
            skLineSegment(sketch, "E11.14.0.1", {"start": v(-142, 38) * mm, "end": v(-142, 13.4) * mm});
            skLineSegment(sketch, "E11.14.0.2", {"start": v(-138, 38) * mm, "end": v(-138, 13.4) * mm});
            skArc(sketch, "E11.14.0.3", {"start": v(-142, 13.4) * mm, "mid": v(-140, 11.4) * mm, "end": v(-138, 13.4) * mm});
            skLineSegment(sketch, "E11.15.0.0", {"start": v(-152, 38) * mm, "end": v(-148, 38) * mm});
            skLineSegment(sketch, "E11.15.0.1", {"start": v(-152, 38) * mm, "end": v(-152, 13.4) * mm});
            skLineSegment(sketch, "E11.15.0.2", {"start": v(-148, 38) * mm, "end": v(-148, 13.4) * mm});
            skArc(sketch, "E11.15.0.3", {"start": v(-152, 13.4) * mm, "mid": v(-150, 11.4) * mm, "end": v(-148, 13.4) * mm});
            skLineSegment(sketch, "E11.16.0.0", {"start": v(-162, 38) * mm, "end": v(-158, 38) * mm});
            skLineSegment(sketch, "E11.16.0.1", {"start": v(-162, 38) * mm, "end": v(-162, 13.4) * mm});
            skLineSegment(sketch, "E11.16.0.2", {"start": v(-158, 38) * mm, "end": v(-158, 13.4) * mm});
            skArc(sketch, "E11.16.0.3", {"start": v(-162, 13.4) * mm, "mid": v(-160, 11.4) * mm, "end": v(-158, 13.4) * mm});
            skLineSegment(sketch, "E11.17.0.0", {"start": v(-172, 38) * mm, "end": v(-168, 38) * mm});
            skLineSegment(sketch, "E11.17.0.1", {"start": v(-172, 38) * mm, "end": v(-172, 13.4) * mm});
            skLineSegment(sketch, "E11.17.0.2", {"start": v(-168, 38) * mm, "end": v(-168, 13.4) * mm});
            skArc(sketch, "E11.17.0.3", {"start": v(-172, 13.4) * mm, "mid": v(-170, 11.4) * mm, "end": v(-168, 13.4) * mm});
            skLineSegment(sketch, "E11.18.0.0", {"start": v(-182, 38) * mm, "end": v(-178, 38) * mm});
            skLineSegment(sketch, "E11.18.0.1", {"start": v(-182, 38) * mm, "end": v(-182, 13.4) * mm});
            skLineSegment(sketch, "E11.18.0.2", {"start": v(-178, 38) * mm, "end": v(-178, 13.4) * mm});
            skArc(sketch, "E11.18.0.3", {"start": v(-182, 13.4) * mm, "mid": v(-180, 11.4) * mm, "end": v(-178, 13.4) * mm});
            skLineSegment(sketch, "E11.19.0.0", {"start": v(-192, 38) * mm, "end": v(-188, 38) * mm});
            skLineSegment(sketch, "E11.19.0.1", {"start": v(-192, 38) * mm, "end": v(-192, 13.4) * mm});
            skLineSegment(sketch, "E11.19.0.2", {"start": v(-188, 38) * mm, "end": v(-188, 13.4) * mm});
            skArc(sketch, "E11.19.0.3", {"start": v(-192, 13.4) * mm, "mid": v(-190, 11.4) * mm, "end": v(-188, 13.4) * mm});
            skLineSegment(sketch, "E11.20.0.0", {"start": v(-202, 38) * mm, "end": v(-198, 38) * mm});
            skLineSegment(sketch, "E11.20.0.1", {"start": v(-202, 38) * mm, "end": v(-202, 13.4) * mm});
            skLineSegment(sketch, "E11.20.0.2", {"start": v(-198, 38) * mm, "end": v(-198, 13.4) * mm});
            skArc(sketch, "E11.20.0.3", {"start": v(-202, 13.4) * mm, "mid": v(-200, 11.4) * mm, "end": v(-198, 13.4) * mm});
            skLineSegment(sketch, "E11.21.0.0", {"start": v(-212, 38) * mm, "end": v(-208, 38) * mm});
            skLineSegment(sketch, "E11.21.0.1", {"start": v(-212, 38) * mm, "end": v(-212, 13.4) * mm});
            skLineSegment(sketch, "E11.21.0.2", {"start": v(-208, 38) * mm, "end": v(-208, 13.4) * mm});
            skArc(sketch, "E11.21.0.3", {"start": v(-212, 13.4) * mm, "mid": v(-210, 11.4) * mm, "end": v(-208, 13.4) * mm});
            skLineSegment(sketch, "E11.22.0.0", {"start": v(-222, 38) * mm, "end": v(-218, 38) * mm});
            skLineSegment(sketch, "E11.22.0.1", {"start": v(-222, 38) * mm, "end": v(-222, 13.4) * mm});
            skLineSegment(sketch, "E11.22.0.2", {"start": v(-218, 38) * mm, "end": v(-218, 13.4) * mm});
            skArc(sketch, "E11.22.0.3", {"start": v(-222, 13.4) * mm, "mid": v(-220, 11.4) * mm, "end": v(-218, 13.4) * mm});
            skLineSegment(sketch, "E11.23.0.0", {"start": v(-232, 38) * mm, "end": v(-228, 38) * mm});
            skLineSegment(sketch, "E11.23.0.1", {"start": v(-232, 38) * mm, "end": v(-232, 13.4) * mm});
            skLineSegment(sketch, "E11.23.0.2", {"start": v(-228, 38) * mm, "end": v(-228, 13.4) * mm});
            skArc(sketch, "E11.23.0.3", {"start": v(-232, 13.4) * mm, "mid": v(-230, 11.4) * mm, "end": v(-228, 13.4) * mm});
            skLineSegment(sketch, "E11.24.0.0", {"start": v(-242, 38) * mm, "end": v(-238, 38) * mm});
            skLineSegment(sketch, "E11.24.0.1", {"start": v(-242, 38) * mm, "end": v(-242, 13.4) * mm});
            skLineSegment(sketch, "E11.24.0.2", {"start": v(-238, 38) * mm, "end": v(-238, 13.4) * mm});
            skArc(sketch, "E11.24.0.3", {"start": v(-242, 13.4) * mm, "mid": v(-240, 11.4) * mm, "end": v(-238, 13.4) * mm});
            skLineSegment(sketch, "E11.25.0.0", {"start": v(-252, 38) * mm, "end": v(-248, 38) * mm});
            skLineSegment(sketch, "E11.25.0.1", {"start": v(-252, 38) * mm, "end": v(-252, 13.4) * mm});
            skLineSegment(sketch, "E11.25.0.2", {"start": v(-248, 38) * mm, "end": v(-248, 13.4) * mm});
            skArc(sketch, "E11.25.0.3", {"start": v(-252, 13.4) * mm, "mid": v(-250, 11.4) * mm, "end": v(-248, 13.4) * mm});
            skLineSegment(sketch, "E11.26.0.0", {"start": v(-262, 38) * mm, "end": v(-258, 38) * mm});
            skLineSegment(sketch, "E11.26.0.1", {"start": v(-262, 38) * mm, "end": v(-262, 13.4) * mm});
            skLineSegment(sketch, "E11.26.0.2", {"start": v(-258, 38) * mm, "end": v(-258, 13.4) * mm});
            skArc(sketch, "E11.26.0.3", {"start": v(-262, 13.4) * mm, "mid": v(-260, 11.4) * mm, "end": v(-258, 13.4) * mm});
            skLineSegment(sketch, "E11.27.0.0", {"start": v(-272, 38) * mm, "end": v(-268, 38) * mm});
            skLineSegment(sketch, "E11.27.0.1", {"start": v(-272, 38) * mm, "end": v(-272, 13.4) * mm});
            skLineSegment(sketch, "E11.27.0.2", {"start": v(-268, 38) * mm, "end": v(-268, 13.4) * mm});
            skArc(sketch, "E11.27.0.3", {"start": v(-272, 13.4) * mm, "mid": v(-270, 11.4) * mm, "end": v(-268, 13.4) * mm});
            skLineSegment(sketch, "E11.28.0.0", {"start": v(-282, 38) * mm, "end": v(-278, 38) * mm});
            skLineSegment(sketch, "E11.28.0.1", {"start": v(-282, 38) * mm, "end": v(-282, 13.4) * mm});
            skLineSegment(sketch, "E11.28.0.2", {"start": v(-278, 38) * mm, "end": v(-278, 13.4) * mm});
            skArc(sketch, "E11.28.0.3", {"start": v(-282, 13.4) * mm, "mid": v(-280, 11.4) * mm, "end": v(-278, 13.4) * mm});
            skLineSegment(sketch, "E11.29.0.0", {"start": v(-292, 38) * mm, "end": v(-288, 38) * mm});
            skLineSegment(sketch, "E11.29.0.1", {"start": v(-292, 38) * mm, "end": v(-292, 13.4) * mm});
            skLineSegment(sketch, "E11.29.0.2", {"start": v(-288, 38) * mm, "end": v(-288, 13.4) * mm});
            skArc(sketch, "E11.29.0.3", {"start": v(-292, 13.4) * mm, "mid": v(-290, 11.4) * mm, "end": v(-288, 13.4) * mm});
            skLineSegment(sketch, "E11.30.0.0", {"start": v(-302, 38) * mm, "end": v(-298, 38) * mm});
            skLineSegment(sketch, "E11.30.0.1", {"start": v(-302, 38) * mm, "end": v(-302, 13.4) * mm});
            skLineSegment(sketch, "E11.30.0.2", {"start": v(-298, 38) * mm, "end": v(-298, 13.4) * mm});
            skArc(sketch, "E11.30.0.3", {"start": v(-302, 13.4) * mm, "mid": v(-300, 11.4) * mm, "end": v(-298, 13.4) * mm});
            skLineSegment(sketch, "E11.31.0.0", {"start": v(-312, 38) * mm, "end": v(-308, 38) * mm});
            skLineSegment(sketch, "E11.31.0.1", {"start": v(-312, 38) * mm, "end": v(-312, 13.4) * mm});
            skLineSegment(sketch, "E11.31.0.2", {"start": v(-308, 38) * mm, "end": v(-308, 13.4) * mm});
            skArc(sketch, "E11.31.0.3", {"start": v(-312, 13.4) * mm, "mid": v(-310, 11.4) * mm, "end": v(-308, 13.4) * mm});
            skLineSegment(sketch, "E11.32.0.0", {"start": v(-322, 38) * mm, "end": v(-318, 38) * mm});
            skLineSegment(sketch, "E11.32.0.1", {"start": v(-322, 38) * mm, "end": v(-322, 13.4) * mm});
            skLineSegment(sketch, "E11.32.0.2", {"start": v(-318, 38) * mm, "end": v(-318, 13.4) * mm});
            skArc(sketch, "E11.32.0.3", {"start": v(-322, 13.4) * mm, "mid": v(-320, 11.4) * mm, "end": v(-318, 13.4) * mm});
            skLineSegment(sketch, "E11.33.0.0", {"start": v(-332, 38) * mm, "end": v(-328, 38) * mm});
            skLineSegment(sketch, "E11.33.0.1", {"start": v(-332, 38) * mm, "end": v(-332, 13.4) * mm});
            skLineSegment(sketch, "E11.33.0.2", {"start": v(-328, 38) * mm, "end": v(-328, 13.4) * mm});
            skArc(sketch, "E11.33.0.3", {"start": v(-332, 13.4) * mm, "mid": v(-330, 11.4) * mm, "end": v(-328, 13.4) * mm});
            skLineSegment(sketch, "E11.34.0.0", {"start": v(-342, 38) * mm, "end": v(-338, 38) * mm});
            skLineSegment(sketch, "E11.34.0.1", {"start": v(-342, 38) * mm, "end": v(-342, 13.4) * mm});
            skLineSegment(sketch, "E11.34.0.2", {"start": v(-338, 38) * mm, "end": v(-338, 13.4) * mm});
            skArc(sketch, "E11.34.0.3", {"start": v(-342, 13.4) * mm, "mid": v(-340, 11.4) * mm, "end": v(-338, 13.4) * mm});
            skLineSegment(sketch, "E11.35.0.0", {"start": v(-352, 38) * mm, "end": v(-348, 38) * mm});
            skLineSegment(sketch, "E11.35.0.1", {"start": v(-352, 38) * mm, "end": v(-352, 13.4) * mm});
            skLineSegment(sketch, "E11.35.0.2", {"start": v(-348, 38) * mm, "end": v(-348, 13.4) * mm});
            skArc(sketch, "E11.35.0.3", {"start": v(-352, 13.4) * mm, "mid": v(-350, 11.4) * mm, "end": v(-348, 13.4) * mm});
            skLineSegment(sketch, "E11.36.0.0", {"start": v(-362, 38) * mm, "end": v(-358, 38) * mm});
            skLineSegment(sketch, "E11.36.0.1", {"start": v(-362, 38) * mm, "end": v(-362, 13.4) * mm});
            skLineSegment(sketch, "E11.36.0.2", {"start": v(-358, 38) * mm, "end": v(-358, 13.4) * mm});
            skArc(sketch, "E11.36.0.3", {"start": v(-362, 13.4) * mm, "mid": v(-360, 11.4) * mm, "end": v(-358, 13.4) * mm});
            skLineSegment(sketch, "E11.37.0.0", {"start": v(-372, 38) * mm, "end": v(-368, 38) * mm});
            skLineSegment(sketch, "E11.37.0.1", {"start": v(-372, 38) * mm, "end": v(-372, 13.4) * mm});
            skLineSegment(sketch, "E11.37.0.2", {"start": v(-368, 38) * mm, "end": v(-368, 13.4) * mm});
            skArc(sketch, "E11.37.0.3", {"start": v(-372, 13.4) * mm, "mid": v(-370, 11.4) * mm, "end": v(-368, 13.4) * mm});
            skLineSegment(sketch, "E11.38.0.0", {"start": v(-382, 38) * mm, "end": v(-378, 38) * mm});
            skLineSegment(sketch, "E11.38.0.1", {"start": v(-382, 38) * mm, "end": v(-382, 13.4) * mm});
            skLineSegment(sketch, "E11.38.0.2", {"start": v(-378, 38) * mm, "end": v(-378, 13.4) * mm});
            skArc(sketch, "E11.38.0.3", {"start": v(-382, 13.4) * mm, "mid": v(-380, 11.4) * mm, "end": v(-378, 13.4) * mm});
            skLineSegment(sketch, "E11.39.0.0", {"start": v(-392, 38) * mm, "end": v(-388, 38) * mm});
            skLineSegment(sketch, "E11.39.0.1", {"start": v(-392, 38) * mm, "end": v(-392, 13.4) * mm});
            skLineSegment(sketch, "E11.39.0.2", {"start": v(-388, 38) * mm, "end": v(-388, 13.4) * mm});
            skArc(sketch, "E11.39.0.3", {"start": v(-392, 13.4) * mm, "mid": v(-390, 11.4) * mm, "end": v(-388, 13.4) * mm});
            skLineSegment(sketch, "E11.40.0.0", {"start": v(-402, 38) * mm, "end": v(-398, 38) * mm});
            skLineSegment(sketch, "E11.40.0.1", {"start": v(-402, 38) * mm, "end": v(-402, 13.4) * mm});
            skLineSegment(sketch, "E11.40.0.2", {"start": v(-398, 38) * mm, "end": v(-398, 13.4) * mm});
            skArc(sketch, "E11.40.0.3", {"start": v(-402, 13.4) * mm, "mid": v(-400, 11.4) * mm, "end": v(-398, 13.4) * mm});
            skLineSegment(sketch, "E11.41.0.0", {"start": v(-412, 38) * mm, "end": v(-408, 38) * mm});
            skLineSegment(sketch, "E11.41.0.1", {"start": v(-412, 38) * mm, "end": v(-412, 13.4) * mm});
            skLineSegment(sketch, "E11.41.0.2", {"start": v(-408, 38) * mm, "end": v(-408, 13.4) * mm});
            skArc(sketch, "E11.41.0.3", {"start": v(-412, 13.4) * mm, "mid": v(-410, 11.4) * mm, "end": v(-408, 13.4) * mm});
            skLineSegment(sketch, "E11.42.0.0", {"start": v(-422, 38) * mm, "end": v(-418, 38) * mm});
            skLineSegment(sketch, "E11.42.0.1", {"start": v(-422, 38) * mm, "end": v(-422, 13.4) * mm});
            skLineSegment(sketch, "E11.42.0.2", {"start": v(-418, 38) * mm, "end": v(-418, 13.4) * mm});
            skArc(sketch, "E11.42.0.3", {"start": v(-422, 13.4) * mm, "mid": v(-420, 11.4) * mm, "end": v(-418, 13.4) * mm});
            skLineSegment(sketch, "E11.43.0.0", {"start": v(-432, 38) * mm, "end": v(-428, 38) * mm});
            skLineSegment(sketch, "E11.43.0.1", {"start": v(-432, 38) * mm, "end": v(-432, 13.4) * mm});
            skLineSegment(sketch, "E11.43.0.2", {"start": v(-428, 38) * mm, "end": v(-428, 13.4) * mm});
            skArc(sketch, "E11.43.0.3", {"start": v(-432, 13.4) * mm, "mid": v(-430, 11.4) * mm, "end": v(-428, 13.4) * mm});
            skLineSegment(sketch, "E11.44.0.0", {"start": v(-442, 38) * mm, "end": v(-438, 38) * mm});
            skLineSegment(sketch, "E11.44.0.1", {"start": v(-442, 38) * mm, "end": v(-442, 13.4) * mm});
            skLineSegment(sketch, "E11.44.0.2", {"start": v(-438, 38) * mm, "end": v(-438, 13.4) * mm});
            skArc(sketch, "E11.44.0.3", {"start": v(-442, 13.4) * mm, "mid": v(-440, 11.4) * mm, "end": v(-438, 13.4) * mm});
            skLineSegment(sketch, "E11.45.0.0", {"start": v(-452, 38) * mm, "end": v(-448, 38) * mm});
            skLineSegment(sketch, "E11.45.0.1", {"start": v(-452, 38) * mm, "end": v(-452, 13.4) * mm});
            skLineSegment(sketch, "E11.45.0.2", {"start": v(-448, 38) * mm, "end": v(-448, 13.4) * mm});
            skArc(sketch, "E11.45.0.3", {"start": v(-452, 13.4) * mm, "mid": v(-450, 11.4) * mm, "end": v(-448, 13.4) * mm});
            skLineSegment(sketch, "E11.46.0.0", {"start": v(-462, 38) * mm, "end": v(-458, 38) * mm});
            skLineSegment(sketch, "E11.46.0.1", {"start": v(-462, 38) * mm, "end": v(-462, 13.4) * mm});
            skLineSegment(sketch, "E11.46.0.2", {"start": v(-458, 38) * mm, "end": v(-458, 13.4) * mm});
            skArc(sketch, "E11.46.0.3", {"start": v(-462, 13.4) * mm, "mid": v(-460, 11.4) * mm, "end": v(-458, 13.4) * mm});
            skLineSegment(sketch, "E11.47.0.0", {"start": v(-472, 38) * mm, "end": v(-468, 38) * mm});
            skLineSegment(sketch, "E11.47.0.1", {"start": v(-472, 38) * mm, "end": v(-472, 13.4) * mm});
            skLineSegment(sketch, "E11.47.0.2", {"start": v(-468, 38) * mm, "end": v(-468, 13.4) * mm});
            skArc(sketch, "E11.47.0.3", {"start": v(-472, 13.4) * mm, "mid": v(-470, 11.4) * mm, "end": v(-468, 13.4) * mm});
            skLineSegment(sketch, "E11.48.0.0", {"start": v(-482, 38) * mm, "end": v(-478, 38) * mm});
            skLineSegment(sketch, "E11.48.0.1", {"start": v(-482, 38) * mm, "end": v(-482, 13.4) * mm});
            skLineSegment(sketch, "E11.48.0.2", {"start": v(-478, 38) * mm, "end": v(-478, 13.4) * mm});
            skArc(sketch, "E11.48.0.3", {"start": v(-482, 13.4) * mm, "mid": v(-480, 11.4) * mm, "end": v(-478, 13.4) * mm});
            skLineSegment(sketch, "E11.49.0.0", {"start": v(-492, 38) * mm, "end": v(-488, 38) * mm});
            skLineSegment(sketch, "E11.49.0.1", {"start": v(-492, 38) * mm, "end": v(-492, 13.4) * mm});
            skLineSegment(sketch, "E11.49.0.2", {"start": v(-488, 38) * mm, "end": v(-488, 13.4) * mm});
            skArc(sketch, "E11.49.0.3", {"start": v(-492, 13.4) * mm, "mid": v(-490, 11.4) * mm, "end": v(-488, 13.4) * mm});
            skLineSegment(sketch, "E11.direction1", {"start": v(-2, 38) * mm, "end": v(-12, 38) * mm, "construction": true});
            skLineSegment(sketch, "E12.0.50.0", {"start": v(498, 38) * mm, "end": v(502, 38) * mm});
            skLineSegment(sketch, "E12.3.50.0", {"start": v(498, 38) * mm, "end": v(498, 13.4) * mm});
            skLineSegment(sketch, "E12.6.50.0", {"start": v(502, 38) * mm, "end": v(502, 13.4) * mm});
            skArc(sketch, "E12.9.50.0", {"start": v(498, 13.4) * mm, "mid": v(500, 11.4) * mm, "end": v(502, 13.4) * mm});
            skLineSegment(sketch, "E12.0.51.0", {"start": v(508, 38) * mm, "end": v(512, 38) * mm});
            skLineSegment(sketch, "E12.3.51.0", {"start": v(508, 38) * mm, "end": v(508, 13.4) * mm});
            skLineSegment(sketch, "E12.6.51.0", {"start": v(512, 38) * mm, "end": v(512, 13.4) * mm});
            skArc(sketch, "E12.9.51.0", {"start": v(508, 13.4) * mm, "mid": v(510, 11.4) * mm, "end": v(512, 13.4) * mm});
            skLineSegment(sketch, "E12.0.52.0", {"start": v(518, 38) * mm, "end": v(522, 38) * mm});
            skLineSegment(sketch, "E12.3.52.0", {"start": v(518, 38) * mm, "end": v(518, 13.4) * mm});
            skLineSegment(sketch, "E12.6.52.0", {"start": v(522, 38) * mm, "end": v(522, 13.4) * mm});
            skArc(sketch, "E12.9.52.0", {"start": v(518, 13.4) * mm, "mid": v(520, 11.4) * mm, "end": v(522, 13.4) * mm});
            skLineSegment(sketch, "E12.0.53.0", {"start": v(528, 38) * mm, "end": v(532, 38) * mm});
            skLineSegment(sketch, "E12.3.53.0", {"start": v(528, 38) * mm, "end": v(528, 13.4) * mm});
            skLineSegment(sketch, "E12.6.53.0", {"start": v(532, 38) * mm, "end": v(532, 13.4) * mm});
            skArc(sketch, "E12.9.53.0", {"start": v(528, 13.4) * mm, "mid": v(530, 11.4) * mm, "end": v(532, 13.4) * mm});
            skLineSegment(sketch, "E12.0.54.0", {"start": v(538, 38) * mm, "end": v(542, 38) * mm});
            skLineSegment(sketch, "E12.3.54.0", {"start": v(538, 38) * mm, "end": v(538, 13.4) * mm});
            skLineSegment(sketch, "E12.6.54.0", {"start": v(542, 38) * mm, "end": v(542, 13.4) * mm});
            skArc(sketch, "E12.9.54.0", {"start": v(538, 13.4) * mm, "mid": v(540, 11.4) * mm, "end": v(542, 13.4) * mm});
            skLineSegment(sketch, "E12.0.55.0", {"start": v(548, 38) * mm, "end": v(552, 38) * mm});
            skLineSegment(sketch, "E12.3.55.0", {"start": v(548, 38) * mm, "end": v(548, 13.4) * mm});
            skLineSegment(sketch, "E12.6.55.0", {"start": v(552, 38) * mm, "end": v(552, 13.4) * mm});
            skArc(sketch, "E12.9.55.0", {"start": v(548, 13.4) * mm, "mid": v(550, 11.4) * mm, "end": v(552, 13.4) * mm});
            skLineSegment(sketch, "E12.0.56.0", {"start": v(558, 38) * mm, "end": v(562, 38) * mm});
            skLineSegment(sketch, "E12.3.56.0", {"start": v(558, 38) * mm, "end": v(558, 13.4) * mm});
            skLineSegment(sketch, "E12.6.56.0", {"start": v(562, 38) * mm, "end": v(562, 13.4) * mm});
            skArc(sketch, "E12.9.56.0", {"start": v(558, 13.4) * mm, "mid": v(560, 11.4) * mm, "end": v(562, 13.4) * mm});
            skLineSegment(sketch, "E12.0.57.0", {"start": v(568, 38) * mm, "end": v(572, 38) * mm});
            skLineSegment(sketch, "E12.3.57.0", {"start": v(568, 38) * mm, "end": v(568, 13.4) * mm});
            skLineSegment(sketch, "E12.6.57.0", {"start": v(572, 38) * mm, "end": v(572, 13.4) * mm});
            skArc(sketch, "E12.9.57.0", {"start": v(568, 13.4) * mm, "mid": v(570, 11.4) * mm, "end": v(572, 13.4) * mm});
            skLineSegment(sketch, "E12.0.58.0", {"start": v(578, 38) * mm, "end": v(582, 38) * mm});
            skLineSegment(sketch, "E12.3.58.0", {"start": v(578, 38) * mm, "end": v(578, 13.4) * mm});
            skLineSegment(sketch, "E12.6.58.0", {"start": v(582, 38) * mm, "end": v(582, 13.4) * mm});
            skArc(sketch, "E12.9.58.0", {"start": v(578, 13.4) * mm, "mid": v(580, 11.4) * mm, "end": v(582, 13.4) * mm});
            skLineSegment(sketch, "E12.0.59.0", {"start": v(588, 38) * mm, "end": v(592, 38) * mm});
            skLineSegment(sketch, "E12.3.59.0", {"start": v(588, 38) * mm, "end": v(588, 13.4) * mm});
            skLineSegment(sketch, "E12.6.59.0", {"start": v(592, 38) * mm, "end": v(592, 13.4) * mm});
            skArc(sketch, "E12.9.59.0", {"start": v(588, 13.4) * mm, "mid": v(590, 11.4) * mm, "end": v(592, 13.4) * mm});
            skLineSegment(sketch, "E13.0.60.0", {"start": v(598, 38) * mm, "end": v(602, 38) * mm});
            skLineSegment(sketch, "E13.3.60.0", {"start": v(598, 38) * mm, "end": v(598, 13.4) * mm});
            skLineSegment(sketch, "E13.6.60.0", {"start": v(602, 38) * mm, "end": v(602, 13.4) * mm});
            skArc(sketch, "E13.9.60.0", {"start": v(598, 13.4) * mm, "mid": v(600, 11.4) * mm, "end": v(602, 13.4) * mm});
            skLineSegment(sketch, "E13.0.61.0", {"start": v(608, 38) * mm, "end": v(612, 38) * mm});
            skLineSegment(sketch, "E13.3.61.0", {"start": v(608, 38) * mm, "end": v(608, 13.4) * mm});
            skLineSegment(sketch, "E13.6.61.0", {"start": v(612, 38) * mm, "end": v(612, 13.4) * mm});
            skArc(sketch, "E13.9.61.0", {"start": v(608, 13.4) * mm, "mid": v(610, 11.4) * mm, "end": v(612, 13.4) * mm});
            skLineSegment(sketch, "E14.0.50.0", {"start": v(-502, 38) * mm, "end": v(-498, 38) * mm});
            skLineSegment(sketch, "E14.3.50.0", {"start": v(-502, 38) * mm, "end": v(-502, 13.4) * mm});
            skLineSegment(sketch, "E14.6.50.0", {"start": v(-498, 38) * mm, "end": v(-498, 13.4) * mm});
            skArc(sketch, "E14.9.50.0", {"start": v(-502, 13.4) * mm, "mid": v(-500, 11.4) * mm, "end": v(-498, 13.4) * mm});
            skLineSegment(sketch, "E14.0.51.0", {"start": v(-512, 38) * mm, "end": v(-508, 38) * mm});
            skLineSegment(sketch, "E14.3.51.0", {"start": v(-512, 38) * mm, "end": v(-512, 13.4) * mm});
            skLineSegment(sketch, "E14.6.51.0", {"start": v(-508, 38) * mm, "end": v(-508, 13.4) * mm});
            skArc(sketch, "E14.9.51.0", {"start": v(-512, 13.4) * mm, "mid": v(-510, 11.4) * mm, "end": v(-508, 13.4) * mm});
            skLineSegment(sketch, "E14.0.52.0", {"start": v(-522, 38) * mm, "end": v(-518, 38) * mm});
            skLineSegment(sketch, "E14.3.52.0", {"start": v(-522, 38) * mm, "end": v(-522, 13.4) * mm});
            skLineSegment(sketch, "E14.6.52.0", {"start": v(-518, 38) * mm, "end": v(-518, 13.4) * mm});
            skArc(sketch, "E14.9.52.0", {"start": v(-522, 13.4) * mm, "mid": v(-520, 11.4) * mm, "end": v(-518, 13.4) * mm});
            skLineSegment(sketch, "E14.0.53.0", {"start": v(-532, 38) * mm, "end": v(-528, 38) * mm});
            skLineSegment(sketch, "E14.3.53.0", {"start": v(-532, 38) * mm, "end": v(-532, 13.4) * mm});
            skLineSegment(sketch, "E14.6.53.0", {"start": v(-528, 38) * mm, "end": v(-528, 13.4) * mm});
            skArc(sketch, "E14.9.53.0", {"start": v(-532, 13.4) * mm, "mid": v(-530, 11.4) * mm, "end": v(-528, 13.4) * mm});
            skLineSegment(sketch, "E14.0.54.0", {"start": v(-542, 38) * mm, "end": v(-538, 38) * mm});
            skLineSegment(sketch, "E14.3.54.0", {"start": v(-542, 38) * mm, "end": v(-542, 13.4) * mm});
            skLineSegment(sketch, "E14.6.54.0", {"start": v(-538, 38) * mm, "end": v(-538, 13.4) * mm});
            skArc(sketch, "E14.9.54.0", {"start": v(-542, 13.4) * mm, "mid": v(-540, 11.4) * mm, "end": v(-538, 13.4) * mm});
            skLineSegment(sketch, "E14.0.55.0", {"start": v(-552, 38) * mm, "end": v(-548, 38) * mm});
            skLineSegment(sketch, "E14.3.55.0", {"start": v(-552, 38) * mm, "end": v(-552, 13.4) * mm});
            skLineSegment(sketch, "E14.6.55.0", {"start": v(-548, 38) * mm, "end": v(-548, 13.4) * mm});
            skArc(sketch, "E14.9.55.0", {"start": v(-552, 13.4) * mm, "mid": v(-550, 11.4) * mm, "end": v(-548, 13.4) * mm});
            skLineSegment(sketch, "E14.0.56.0", {"start": v(-562, 38) * mm, "end": v(-558, 38) * mm});
            skLineSegment(sketch, "E14.3.56.0", {"start": v(-562, 38) * mm, "end": v(-562, 13.4) * mm});
            skLineSegment(sketch, "E14.6.56.0", {"start": v(-558, 38) * mm, "end": v(-558, 13.4) * mm});
            skArc(sketch, "E14.9.56.0", {"start": v(-562, 13.4) * mm, "mid": v(-560, 11.4) * mm, "end": v(-558, 13.4) * mm});
            skLineSegment(sketch, "E14.0.57.0", {"start": v(-572, 38) * mm, "end": v(-568, 38) * mm});
            skLineSegment(sketch, "E14.3.57.0", {"start": v(-572, 38) * mm, "end": v(-572, 13.4) * mm});
            skLineSegment(sketch, "E14.6.57.0", {"start": v(-568, 38) * mm, "end": v(-568, 13.4) * mm});
            skArc(sketch, "E14.9.57.0", {"start": v(-572, 13.4) * mm, "mid": v(-570, 11.4) * mm, "end": v(-568, 13.4) * mm});
            skLineSegment(sketch, "E14.0.58.0", {"start": v(-582, 38) * mm, "end": v(-578, 38) * mm});
            skLineSegment(sketch, "E14.3.58.0", {"start": v(-582, 38) * mm, "end": v(-582, 13.4) * mm});
            skLineSegment(sketch, "E14.6.58.0", {"start": v(-578, 38) * mm, "end": v(-578, 13.4) * mm});
            skArc(sketch, "E14.9.58.0", {"start": v(-582, 13.4) * mm, "mid": v(-580, 11.4) * mm, "end": v(-578, 13.4) * mm});
            skLineSegment(sketch, "E14.0.59.0", {"start": v(-592, 38) * mm, "end": v(-588, 38) * mm});
            skLineSegment(sketch, "E14.3.59.0", {"start": v(-592, 38) * mm, "end": v(-592, 13.4) * mm});
            skLineSegment(sketch, "E14.6.59.0", {"start": v(-588, 38) * mm, "end": v(-588, 13.4) * mm});
            skArc(sketch, "E14.9.59.0", {"start": v(-592, 13.4) * mm, "mid": v(-590, 11.4) * mm, "end": v(-588, 13.4) * mm});
            skLineSegment(sketch, "E14.0.60.0", {"start": v(-602, 38) * mm, "end": v(-598, 38) * mm});
            skLineSegment(sketch, "E14.3.60.0", {"start": v(-602, 38) * mm, "end": v(-602, 13.4) * mm});
            skLineSegment(sketch, "E14.6.60.0", {"start": v(-598, 38) * mm, "end": v(-598, 13.4) * mm});
            skArc(sketch, "E14.9.60.0", {"start": v(-602, 13.4) * mm, "mid": v(-600, 11.4) * mm, "end": v(-598, 13.4) * mm});
            skLineSegment(sketch, "E14.0.61.0", {"start": v(-612, 38) * mm, "end": v(-608, 38) * mm});
            skLineSegment(sketch, "E14.3.61.0", {"start": v(-612, 38) * mm, "end": v(-612, 13.4) * mm});
            skLineSegment(sketch, "E14.6.61.0", {"start": v(-608, 38) * mm, "end": v(-608, 13.4) * mm});
            skArc(sketch, "E14.9.61.0", {"start": v(-612, 13.4) * mm, "mid": v(-610, 11.4) * mm, "end": v(-608, 13.4) * mm});
            skSolve(sketch);
        }
        {
            var Q0;
            Q0 = qSketchRegion(id + "F2", true);
            extrude(context, id + "F3", {"entities" : qUnion([Q0]), "operationType" : NewBodyOperationType.REMOVE, "endBound" : BoundingType.THROUGH_ALL, "oppositeDirection" : true, "depth" : 25 * mm});
        }
        {
            var Q0;
            Q0=makeQuery(id+"F1.opExtrude","SWEPT_FACE",FACE,{"disambiguationData":[OSD([sQuery(id+"F0.wireOp",EDGE,"E3")])]});
            var sketch = newSketch(context, id + "F4", { "sketchPlane" : qUnion([Q0])});
            skLineSegment(sketch, "E15", {"start": v(4.5, 0) * mm, "end": v(-4.5, 0) * mm});
            skArc(sketch, "E16.0.startCap", {"start": v(4.5, 3) * mm, "mid": v(7.5, 0) * mm, "end": v(4.5, -3) * mm});
            skArc(sketch, "E16.0.endCap", {"start": v(-4.5, -3) * mm, "mid": v(-7.5, 0) * mm, "end": v(-4.5, 3) * mm});
            skLineSegment(sketch, "E16.0.left", {"start": v(4.5, -3) * mm, "end": v(-4.5, -3) * mm});
            skLineSegment(sketch, "E16.0.right", {"start": v(4.5, 3) * mm, "end": v(-4.5, 3) * mm});
            skLineSegment(sketch, "E17.1.0.0", {"start": v(104.5, -3) * mm, "end": v(95.5, -3) * mm});
            skArc(sketch, "E17.1.0.1", {"start": v(104.5, 3) * mm, "mid": v(107.5, 0) * mm, "end": v(104.5, -3) * mm});
            skLineSegment(sketch, "E17.1.0.2", {"start": v(104.5, 3) * mm, "end": v(95.5, 3) * mm});
            skArc(sketch, "E17.1.0.3", {"start": v(95.5, -3) * mm, "mid": v(92.5, 0) * mm, "end": v(95.5, 3) * mm});
            skLineSegment(sketch, "E17.2.0.0", {"start": v(204.5, -3) * mm, "end": v(195.5, -3) * mm});
            skArc(sketch, "E17.2.0.1", {"start": v(204.5, 3) * mm, "mid": v(207.5, 0) * mm, "end": v(204.5, -3) * mm});
            skLineSegment(sketch, "E17.2.0.2", {"start": v(204.5, 3) * mm, "end": v(195.5, 3) * mm});
            skArc(sketch, "E17.2.0.3", {"start": v(195.5, -3) * mm, "mid": v(192.5, 0) * mm, "end": v(195.5, 3) * mm});
            skLineSegment(sketch, "E17.3.0.0", {"start": v(304.5, -3) * mm, "end": v(295.5, -3) * mm});
            skArc(sketch, "E17.3.0.1", {"start": v(304.5, 3) * mm, "mid": v(307.5, 0) * mm, "end": v(304.5, -3) * mm});
            skLineSegment(sketch, "E17.3.0.2", {"start": v(304.5, 3) * mm, "end": v(295.5, 3) * mm});
            skArc(sketch, "E17.3.0.3", {"start": v(295.5, -3) * mm, "mid": v(292.5, 0) * mm, "end": v(295.5, 3) * mm});
            skLineSegment(sketch, "E17.4.0.0", {"start": v(404.5, -3) * mm, "end": v(395.5, -3) * mm});
            skArc(sketch, "E17.4.0.1", {"start": v(404.5, 3) * mm, "mid": v(407.5, 0) * mm, "end": v(404.5, -3) * mm});
            skLineSegment(sketch, "E17.4.0.2", {"start": v(404.5, 3) * mm, "end": v(395.5, 3) * mm});
            skArc(sketch, "E17.4.0.3", {"start": v(395.5, -3) * mm, "mid": v(392.5, 0) * mm, "end": v(395.5, 3) * mm});
            skLineSegment(sketch, "E17.5.0.0", {"start": v(504.5, -3) * mm, "end": v(495.5, -3) * mm});
            skArc(sketch, "E17.5.0.1", {"start": v(504.5, 3) * mm, "mid": v(507.5, 0) * mm, "end": v(504.5, -3) * mm});
            skLineSegment(sketch, "E17.5.0.2", {"start": v(504.5, 3) * mm, "end": v(495.5, 3) * mm});
            skArc(sketch, "E17.5.0.3", {"start": v(495.5, -3) * mm, "mid": v(492.5, 0) * mm, "end": v(495.5, 3) * mm});
            skLineSegment(sketch, "E17.direction1", {"start": v(-4.5, -3) * mm, "end": v(95.5, -3) * mm, "construction": true});
            skArc(sketch, "E18.1.0.0", {"start": v(-95.5, 3) * mm, "mid": v(-92.5, 0) * mm, "end": v(-95.5, -3) * mm});
            skLineSegment(sketch, "E18.1.0.1", {"start": v(-95.5, -3) * mm, "end": v(-104.5, -3) * mm});
            skArc(sketch, "E18.1.0.2", {"start": v(-104.5, -3) * mm, "mid": v(-107.5, 0) * mm, "end": v(-104.5, 3) * mm});
            skLineSegment(sketch, "E18.1.0.3", {"start": v(-95.5, 3) * mm, "end": v(-104.5, 3) * mm});
            skArc(sketch, "E18.2.0.0", {"start": v(-195.5, 3) * mm, "mid": v(-192.5, 0) * mm, "end": v(-195.5, -3) * mm});
            skLineSegment(sketch, "E18.2.0.1", {"start": v(-195.5, -3) * mm, "end": v(-204.5, -3) * mm});
            skArc(sketch, "E18.2.0.2", {"start": v(-204.5, -3) * mm, "mid": v(-207.5, 0) * mm, "end": v(-204.5, 3) * mm});
            skLineSegment(sketch, "E18.2.0.3", {"start": v(-195.5, 3) * mm, "end": v(-204.5, 3) * mm});
            skArc(sketch, "E18.3.0.0", {"start": v(-295.5, 3) * mm, "mid": v(-292.5, 0) * mm, "end": v(-295.5, -3) * mm});
            skLineSegment(sketch, "E18.3.0.1", {"start": v(-295.5, -3) * mm, "end": v(-304.5, -3) * mm});
            skArc(sketch, "E18.3.0.2", {"start": v(-304.5, -3) * mm, "mid": v(-307.5, 0) * mm, "end": v(-304.5, 3) * mm});
            skLineSegment(sketch, "E18.3.0.3", {"start": v(-295.5, 3) * mm, "end": v(-304.5, 3) * mm});
            skArc(sketch, "E18.4.0.0", {"start": v(-395.5, 3) * mm, "mid": v(-392.5, 0) * mm, "end": v(-395.5, -3) * mm});
            skLineSegment(sketch, "E18.4.0.1", {"start": v(-395.5, -3) * mm, "end": v(-404.5, -3) * mm});
            skArc(sketch, "E18.4.0.2", {"start": v(-404.5, -3) * mm, "mid": v(-407.5, 0) * mm, "end": v(-404.5, 3) * mm});
            skLineSegment(sketch, "E18.4.0.3", {"start": v(-395.5, 3) * mm, "end": v(-404.5, 3) * mm});
            skArc(sketch, "E18.5.0.0", {"start": v(-495.5, 3) * mm, "mid": v(-492.5, 0) * mm, "end": v(-495.5, -3) * mm});
            skLineSegment(sketch, "E18.5.0.1", {"start": v(-495.5, -3) * mm, "end": v(-504.5, -3) * mm});
            skArc(sketch, "E18.5.0.2", {"start": v(-504.5, -3) * mm, "mid": v(-507.5, 0) * mm, "end": v(-504.5, 3) * mm});
            skLineSegment(sketch, "E18.5.0.3", {"start": v(-495.5, 3) * mm, "end": v(-504.5, 3) * mm});
            skLineSegment(sketch, "E18.direction1", {"start": v(4.5, -3) * mm, "end": v(-95.5, -3) * mm, "construction": true});
            skLineSegment(sketch, "E19.0.6.0", {"start": v(604.5, -3) * mm, "end": v(595.5, -3) * mm});
            skArc(sketch, "E19.3.6.0", {"start": v(604.5, 3) * mm, "mid": v(607.5, 0) * mm, "end": v(604.5, -3) * mm});
            skLineSegment(sketch, "E19.7.6.0", {"start": v(604.5, 3) * mm, "end": v(595.5, 3) * mm});
            skArc(sketch, "E19.10.6.0", {"start": v(595.5, -3) * mm, "mid": v(592.5, 0) * mm, "end": v(595.5, 3) * mm});
            skArc(sketch, "E20.0.6.0", {"start": v(-595.5, 3) * mm, "mid": v(-592.5, 0) * mm, "end": v(-595.5, -3) * mm});
            skLineSegment(sketch, "E20.4.6.0", {"start": v(-595.5, -3) * mm, "end": v(-604.5, -3) * mm});
            skArc(sketch, "E20.7.6.0", {"start": v(-604.5, -3) * mm, "mid": v(-607.5, 0) * mm, "end": v(-604.5, 3) * mm});
            skLineSegment(sketch, "E20.11.6.0", {"start": v(-595.5, 3) * mm, "end": v(-604.5, 3) * mm});
            skSolve(sketch);
        }
        {
            var Q0;
            Q0 = qSketchRegion(id + "F4", true);
            extrude(context, id + "F5", {"entities" : qUnion([Q0]), "operationType" : NewBodyOperationType.REMOVE, "oppositeDirection" : true, "depth" : 25 * mm});
        }
        {
            var Q0;
            Q0=qCreatedBy(makeId("Right.planeOp"),FACE);
            var sketch = newSketch(context, id + "F6", { "sketchPlane" : qUnion([Q0])});
            skLineSegment(sketch, "E21", {"start": v(20, 40) * mm, "end": v(-20, 40) * mm});
            skLineSegment(sketch, "E22", {"start": v(-20, 40) * mm, "end": v(-20, 30) * mm});
            skLineSegment(sketch, "E23", {"start": v(20, 40) * mm, "end": v(20, 30) * mm});
            skLineSegment(sketch, "E24", {"start": v(20, 30) * mm, "end": v(16, 34) * mm});
            skLineSegment(sketch, "E25", {"start": v(16, 34) * mm, "end": v(18, 34) * mm});
            skLineSegment(sketch, "E26", {"start": v(18, 34) * mm, "end": v(18, 38) * mm});
            skLineSegment(sketch, "E27", {"start": v(18, 38) * mm, "end": v(-18, 38) * mm});
            skLineSegment(sketch, "E28", {"start": v(-18, 38) * mm, "end": v(-18, 34) * mm});
            skLineSegment(sketch, "E29", {"start": v(-18, 34) * mm, "end": v(-16, 34) * mm});
            skLineSegment(sketch, "E30", {"start": v(-16, 34) * mm, "end": v(-20, 30) * mm});
            skSolve(sketch);
        }
        {
            var Q0;
            Q0 = qSketchRegion(id + "F6", true);
            extrude(context, id + "F7", {"entities" : qUnion([Q0]), "endBound" : BoundingType.SYMMETRIC, "depth" : 1240 * mm});
        }
        {
            var Q0;
            Q0=makeQuery(id+"F7.opExtrude","SWEPT_EDGE",EDGE,{"disambiguationData":[OSD([sQuery(id+"F6.wireOp",EDGE,"E21"),sQuery(id+"F6.wireOp",EDGE,"E23")])]});
            var Q1;
            Q1=makeQuery(id+"F7.opExtrude","SWEPT_EDGE",EDGE,{"disambiguationData":[OSD([sQuery(id+"F6.wireOp",EDGE,"E21"),sQuery(id+"F6.wireOp",EDGE,"E22")])]});
            var Q2;
            Q2=makeQuery(id+"F1.opExtrude","SWEPT_EDGE",EDGE,{"disambiguationData":[OSD([sQuery(id+"F0.wireOp",EDGE,"E6"),sQuery(id+"F0.wireOp",EDGE,"E7")])]});
            var Q3;
            Q3=makeQuery(id+"F1.opExtrude","SWEPT_EDGE",EDGE,{"disambiguationData":[OSD([sQuery(id+"F0.wireOp",EDGE,"E0"),sQuery(id+"F0.wireOp",EDGE,"E7")])]});
            fillet(context, id + "F8", {"entities" : qUnion([Q0, Q1, Q2, Q3]), "radius" : 1 * mm, "tangentPropagation" : true, "allowEdgeOverflow" : false});
        }
    });
